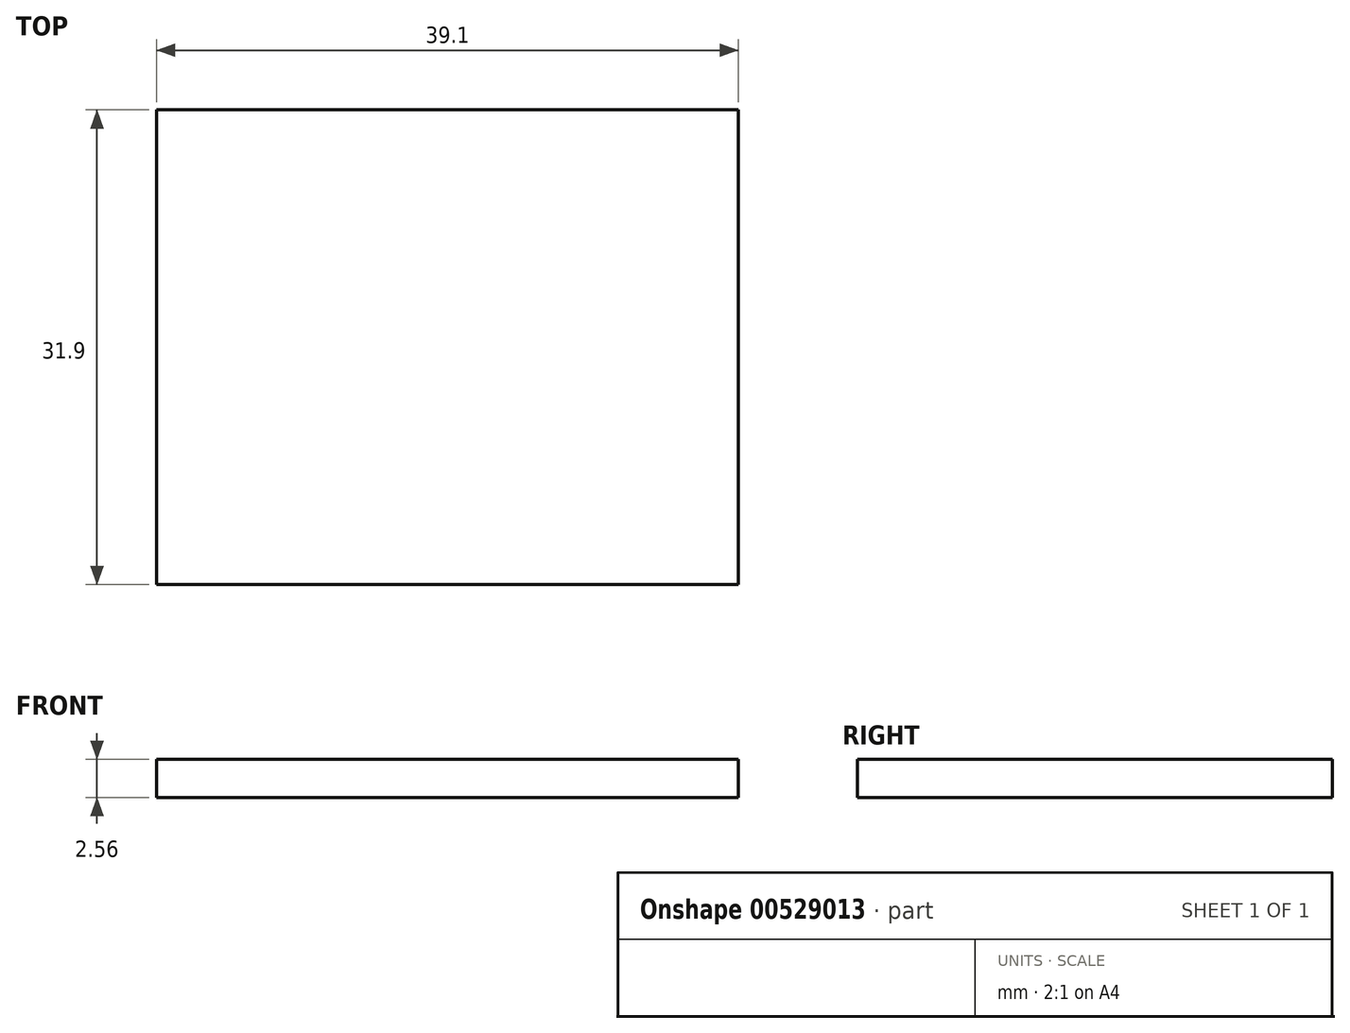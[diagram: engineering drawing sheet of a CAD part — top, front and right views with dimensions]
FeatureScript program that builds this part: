
annotation { "Feature Type Name" : "Feature", "Feature Type Description" : "" }
export const myFeature = defineFeature(function(context is Context, id is Id, definition is map)
    precondition{}
    {
        {
            var Q0;
            Q0=qCreatedBy(makeId("Top.planeOp"),FACE);
            var sketch = newSketch(context, id + "F0", { "sketchPlane" : qUnion([Q0])});
            skLineSegment(sketch, "E0.bottom", {"start": v(0, 0) * mm, "end": v(39.1, 0) * mm});
            skLineSegment(sketch, "E0.top", {"start": v(0, 31.9) * mm, "end": v(39.1, 31.9) * mm});
            skLineSegment(sketch, "E0.left", {"start": v(0, 0) * mm, "end": v(0, 31.9) * mm});
            skLineSegment(sketch, "E0.right", {"start": v(39.1, 0) * mm, "end": v(39.1, 31.9) * mm});
            skSolve(sketch);
        }
        {
            var Q0;
            Q0 = qSketchRegion(id + "F0", true);
            extrude(context, id + "F1", {"entities" : qUnion([Q0]), "depth" : 2.56 * mm, "offsetDistance" : 25.4 * mm});
        }
    });
